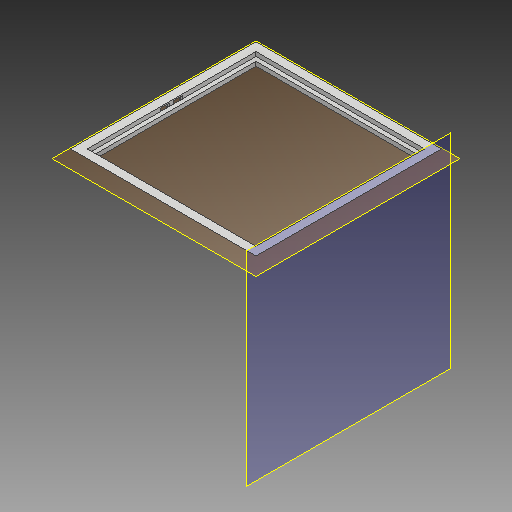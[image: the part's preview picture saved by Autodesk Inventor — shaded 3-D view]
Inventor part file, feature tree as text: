
AUTODESK INVENTOR PART (.ipt)
format: ipt  version: 2018.2 (Build 222227000, 227)  size: 167,936 bytes
history: native  units: mm
features: reference x19, other x10, extrude x4, sketch x4, plane x2, chamfer x1
ambient origin geometry x8: Origin, YZ Plane, XZ Plane, XY Plane, X Axis, Y Axis, Z Axis, Center Point
bodies: Volumenkörper1 (feature_tree)
feature tree (40):
  extrude  "Extrusion1"  Depth=20.0mm TaperAngle=45.0deg
  chamfer  "Fase1"  Distance=17.0mm
  plane  "Arbeitsebene1"
  extrude  "Extrusion2"  Depth=10.0mm
  extrude  "Extrusion3"  Depth=10.0mm
  plane  "Arbeitsebene3"
  extrude  "Extrusion4"  Depth=10.0mm TaperAngle=0.0deg
  sketch  "Skizze1"  dims[d0=20.0mm d1=0.0mm d2=20.0mm d3=2.0mm d4=45.0deg]
  reference  "Referenz1"
  reference  "Referenz2"
  reference  "Referenz3"
  reference  "Referenz4"
  reference  "Referenz5"
  sketch  "Skizze3"  dims[d5=-20.0mm d6=17.0mm d7=0.0mm]
  reference  "Referenz12"
  reference  "Referenz13"
  reference  "Referenz14"
  reference  "Referenz15"
  reference  "Referenz16"
  reference  "Referenz17"
  reference  "Referenz18"
  reference  "Referenz19"
  sketch  "Skizze5"  dims[d8=10.0mm d9=10.0mm]
  sketch  "Skizze6"  dims[d10=10.0mm d11=10.0mm d12=10.0mm d13=0.0mm d14=25.0mm d15=0.0mm]
  reference  "Referenz20"
  reference  "Referenz21"
  reference  "Referenz22"
  reference  "Referenz23"
  reference  "Referenz24"
  reference  "Referenz25"
  parser-record x1  (decoder bookkeeping rows leaked as tree rows — omitted from the tree; the rows remain in map.json)
  other  "SmartCube_Quadratisch.iam"
  other  "Wand2_MIR:1"
  other  "Wand1:1"
  other  "Wand1_MIR:1"
  other  "Wand2:1"
  other  "PV_Modul:1"
  other  "<userpath>\Documents\Dipl\Smartcube_Construction\Version_3\Baugruppe1.iam"
  other  "Baugruppe1.iam"
  other  "PV_Ramen_CPY_3_2:1"
note: 1 file-system path scrubbed to <path> (originals preserved in map.json)
